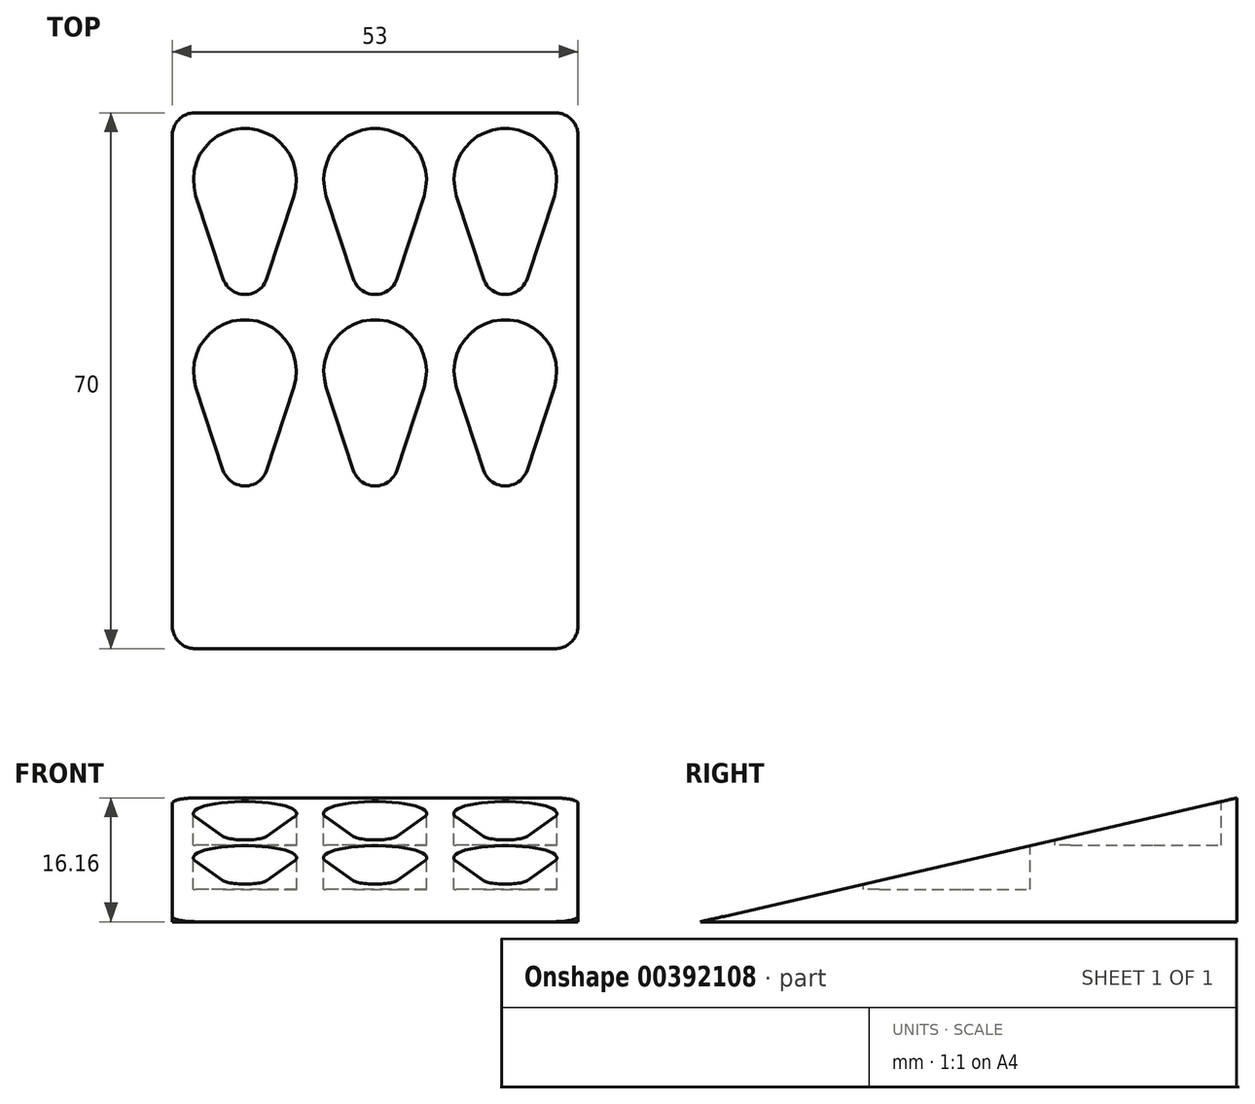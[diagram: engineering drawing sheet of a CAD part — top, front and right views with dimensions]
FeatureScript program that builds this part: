
annotation { "Feature Type Name" : "Feature", "Feature Type Description" : "" }
export const myFeature = defineFeature(function(context is Context, id is Id, definition is map)
    precondition{}
    {
        {
            var Q0;
            Q0=qCreatedBy(makeId("Top.planeOp"),FACE);
            var sketch = newSketch(context, id + "F0", { "sketchPlane" : qUnion([Q0])});
            skLineSegment(sketch, "E0.bottom", {"start": v(-23.5, 35) * mm, "end": v(23.5, 35) * mm});
            skLineSegment(sketch, "E0.top", {"start": v(-23.5, -35) * mm, "end": v(23.5, -35) * mm});
            skLineSegment(sketch, "E0.left", {"start": v(-26.5, 32) * mm, "end": v(-26.5, -32) * mm});
            skLineSegment(sketch, "E0.right", {"start": v(26.5, 32) * mm, "end": v(26.5, -32) * mm});
            skPoint(sketch, "E0.middle", {"position": v(0, 0) * mm});
            skPoint(sketch, "E1.visualSharp", {"position": v(26.5, 35) * mm});
            skArc(sketch, "E1.filletArc", {"start": v(26.5, 32) * mm, "mid": v(25.62, 34.12) * mm, "end": v(23.5, 35) * mm});
            skPoint(sketch, "E2.visualSharp", {"position": v(26.5, -35) * mm});
            skArc(sketch, "E2.filletArc", {"start": v(23.5, -35) * mm, "mid": v(25.62, -34.12) * mm, "end": v(26.5, -32) * mm});
            skPoint(sketch, "E3.visualSharp", {"position": v(-26.5, -35) * mm});
            skArc(sketch, "E3.filletArc", {"start": v(-26.5, -32) * mm, "mid": v(-25.62, -34.12) * mm, "end": v(-23.5, -35) * mm});
            skPoint(sketch, "E4.visualSharp", {"position": v(-26.5, 35) * mm});
            skArc(sketch, "E4.filletArc", {"start": v(-23.5, 35) * mm, "mid": v(-25.62, 34.12) * mm, "end": v(-26.5, 32) * mm});
            skSolve(sketch);
        }
        {
            var Q0;
            Q0 = qSketchRegion(id + "F0", true);
            extrude(context, id + "F1", {"entities" : qUnion([Q0]), "depth" : 25 * mm, "offsetDistance" : 25 * mm});
        }
        {
            var Q0;
            Q0=makeQuery(id+"F1.opExtrude","SWEPT_FACE",FACE,{"disambiguationData":[OSD([sQuery(id+"F0.wireOp",EDGE,"E0.right")])]});
            var sketch = newSketch(context, id + "F2", { "sketchPlane" : qUnion([Q0])});
            skLineSegment(sketch, "E5", {"start": v(-35, 0) * mm, "end": v(35, 16.16) * mm});
            skLineSegment(sketch, "E6", {"start": v(35, 16.16) * mm, "end": v(35, 25) * mm});
            skLineSegment(sketch, "E7", {"start": v(35, 25) * mm, "end": v(-35, 25) * mm});
            skLineSegment(sketch, "E8", {"start": v(-35, 25) * mm, "end": v(-35, 0) * mm});
            skSolve(sketch);
        }
        {
            var Q0;
            Q0 = qSketchRegion(id + "F2", true);
            extrude(context, id + "F3", {"entities" : qUnion([Q0]), "operationType" : NewBodyOperationType.REMOVE, "endBound" : BoundingType.THROUGH_ALL, "oppositeDirection" : true, "depth" : 25 * mm, "offsetDistance" : 25 * mm});
        }
        {
            var Q0;
            Q0=qCreatedBy(makeId("Top.planeOp"),FACE);
            cPlane(context, id + "F4", {"entities" : qUnion([Q0]), "cplaneType" : CPlaneType.OFFSET, "offset" : 25 * mm, "width" : 150 * mm, "height" : 150 * mm});
        }
        {
            var Q0;
            Q0=qCreatedBy(id+"F4.planeOp",FACE);
            var sketch = newSketch(context, id + "F5", { "sketchPlane" : qUnion([Q0])});
            skArc(sketch, "E9", {"start": v(6.41, 24.14) * mm, "mid": v(0, 33) * mm, "end": v(-6.41, 24.14) * mm});
            skArc(sketch, "E10", {"start": v(-2.85, 13.31) * mm, "mid": v(0, 11.25) * mm, "end": v(2.85, 13.31) * mm});
            skLineSegment(sketch, "E11", {"start": v(-2.85, 13.31) * mm, "end": v(-6.41, 24.14) * mm});
            skLineSegment(sketch, "E12", {"start": v(2.85, 13.31) * mm, "end": v(6.41, 24.14) * mm});
            skArc(sketch, "E13.1.0.0", {"start": v(23.41, 24.14) * mm, "mid": v(17, 33) * mm, "end": v(10.59, 24.14) * mm});
            skLineSegment(sketch, "E13.1.0.1", {"start": v(19.85, 13.31) * mm, "end": v(23.41, 24.14) * mm});
            skLineSegment(sketch, "E13.1.0.2", {"start": v(14.15, 13.31) * mm, "end": v(10.59, 24.14) * mm});
            skArc(sketch, "E13.1.0.3", {"start": v(14.15, 13.31) * mm, "mid": v(17, 11.25) * mm, "end": v(19.85, 13.31) * mm});
            skLineSegment(sketch, "E13.direction1", {"start": v(-2.85, 13.31) * mm, "end": v(14.15, 13.31) * mm, "construction": true});
            skLineSegment(sketch, "E14.1.0.0", {"start": v(-14.15, 13.31) * mm, "end": v(-10.59, 24.14) * mm});
            skLineSegment(sketch, "E14.1.0.1", {"start": v(-19.85, 13.31) * mm, "end": v(-23.41, 24.14) * mm});
            skArc(sketch, "E14.1.0.2", {"start": v(-10.59, 24.14) * mm, "mid": v(-17, 33) * mm, "end": v(-23.41, 24.14) * mm});
            skArc(sketch, "E14.1.0.3", {"start": v(-19.85, 13.31) * mm, "mid": v(-17, 11.25) * mm, "end": v(-14.15, 13.31) * mm});
            skLineSegment(sketch, "E14.direction1", {"start": v(-2.85, 13.31) * mm, "end": v(-19.85, 13.31) * mm, "construction": true});
            skLineSegment(sketch, "E15.0.1.0", {"start": v(2.85, -11.69) * mm, "end": v(6.41, -0.86) * mm, "construction": true});
            skArc(sketch, "E15.0.1.1", {"start": v(23.41, -0.86) * mm, "mid": v(17, 8) * mm, "end": v(10.59, -0.86) * mm, "construction": true});
            skLineSegment(sketch, "E15.0.1.2", {"start": v(-2.85, -11.69) * mm, "end": v(-6.41, -0.86) * mm, "construction": true});
            skArc(sketch, "E15.0.1.3", {"start": v(6.41, -0.86) * mm, "mid": v(0, 8) * mm, "end": v(-6.41, -0.86) * mm, "construction": true});
            skLineSegment(sketch, "E15.0.1.4", {"start": v(-2.85, -11.69) * mm, "end": v(-19.85, -11.69) * mm, "construction": true});
            skLineSegment(sketch, "E15.0.1.5", {"start": v(14.15, -11.69) * mm, "end": v(10.59, -0.86) * mm, "construction": true});
            skLineSegment(sketch, "E15.0.1.6", {"start": v(19.85, -11.69) * mm, "end": v(23.41, -0.86) * mm, "construction": true});
            skLineSegment(sketch, "E15.0.1.7", {"start": v(-2.85, -11.69) * mm, "end": v(14.15, -11.69) * mm, "construction": true});
            skLineSegment(sketch, "E15.0.1.8", {"start": v(-14.15, -11.69) * mm, "end": v(-10.59, -0.86) * mm, "construction": true});
            skLineSegment(sketch, "E15.0.1.9", {"start": v(-19.85, -11.69) * mm, "end": v(-23.41, -0.86) * mm, "construction": true});
            skArc(sketch, "E15.0.1.10", {"start": v(-10.59, -0.86) * mm, "mid": v(-17, 8) * mm, "end": v(-23.41, -0.86) * mm, "construction": true});
            skArc(sketch, "E15.0.1.11", {"start": v(-2.85, -11.69) * mm, "mid": v(0, -13.75) * mm, "end": v(2.85, -11.69) * mm, "construction": true});
            skArc(sketch, "E15.0.1.12", {"start": v(14.15, -11.69) * mm, "mid": v(17, -13.75) * mm, "end": v(19.85, -11.69) * mm, "construction": true});
            skArc(sketch, "E15.0.1.13", {"start": v(-19.85, -11.69) * mm, "mid": v(-17, -13.75) * mm, "end": v(-14.15, -11.69) * mm, "construction": true});
            skLineSegment(sketch, "E15.direction1", {"start": v(-19.85, 13.31) * mm, "end": v(5.15, 13.31) * mm, "construction": true});
            skLineSegment(sketch, "E15.direction2", {"start": v(-19.85, 13.31) * mm, "end": v(-19.85, -11.69) * mm, "construction": true});
            skSolve(sketch);
        }
        {
            var Q0;
            Q0 = qSketchRegion(id + "F5", true);
            extrude(context, id + "F6", {"entities" : qUnion([Q0]), "operationType" : NewBodyOperationType.REMOVE, "oppositeDirection" : true, "depth" : 15 * mm, "offsetDistance" : 25 * mm});
        }
        {
            var Q0;
            Q0=qCreatedBy(id+"F4.planeOp",FACE);
            var sketch = newSketch(context, id + "F7", { "sketchPlane" : qUnion([Q0])});
            skArc(sketch, "E16.0", {"start": v(14.15, -11.69) * mm, "mid": v(17, -13.75) * mm, "end": v(19.85, -11.69) * mm});
            skLineSegment(sketch, "E16.1", {"start": v(19.85, -11.69) * mm, "end": v(23.41, -0.86) * mm});
            skArc(sketch, "E16.2", {"start": v(23.41, -0.86) * mm, "mid": v(17, 8) * mm, "end": v(10.59, -0.86) * mm});
            skLineSegment(sketch, "E16.3", {"start": v(14.15, -11.69) * mm, "end": v(10.59, -0.86) * mm});
            skLineSegment(sketch, "E16.4", {"start": v(2.85, -11.69) * mm, "end": v(6.41, -0.86) * mm});
            skArc(sketch, "E16.5", {"start": v(6.41, -0.86) * mm, "mid": v(0, 8) * mm, "end": v(-6.41, -0.86) * mm});
            skLineSegment(sketch, "E16.6", {"start": v(-2.85, -11.69) * mm, "end": v(-6.41, -0.86) * mm});
            skArc(sketch, "E16.7", {"start": v(-2.85, -11.69) * mm, "mid": v(0, -13.75) * mm, "end": v(2.85, -11.69) * mm});
            skLineSegment(sketch, "E16.8", {"start": v(-14.15, -11.69) * mm, "end": v(-10.59, -0.86) * mm});
            skLineSegment(sketch, "E16.9", {"start": v(-19.85, -11.69) * mm, "end": v(-23.41, -0.86) * mm});
            skArc(sketch, "E16.10", {"start": v(-19.85, -11.69) * mm, "mid": v(-17, -13.75) * mm, "end": v(-14.15, -11.69) * mm});
            skArc(sketch, "E16.11", {"start": v(-10.59, -0.86) * mm, "mid": v(-17, 8) * mm, "end": v(-23.41, -0.86) * mm});
            skSolve(sketch);
        }
        {
            var Q0;
            Q0 = qSketchRegion(id + "F7", true);
            extrude(context, id + "F8", {"entities" : qUnion([Q0]), "operationType" : NewBodyOperationType.REMOVE, "oppositeDirection" : true, "depth" : 20.8 * mm, "offsetDistance" : 25 * mm});
        }
    });
